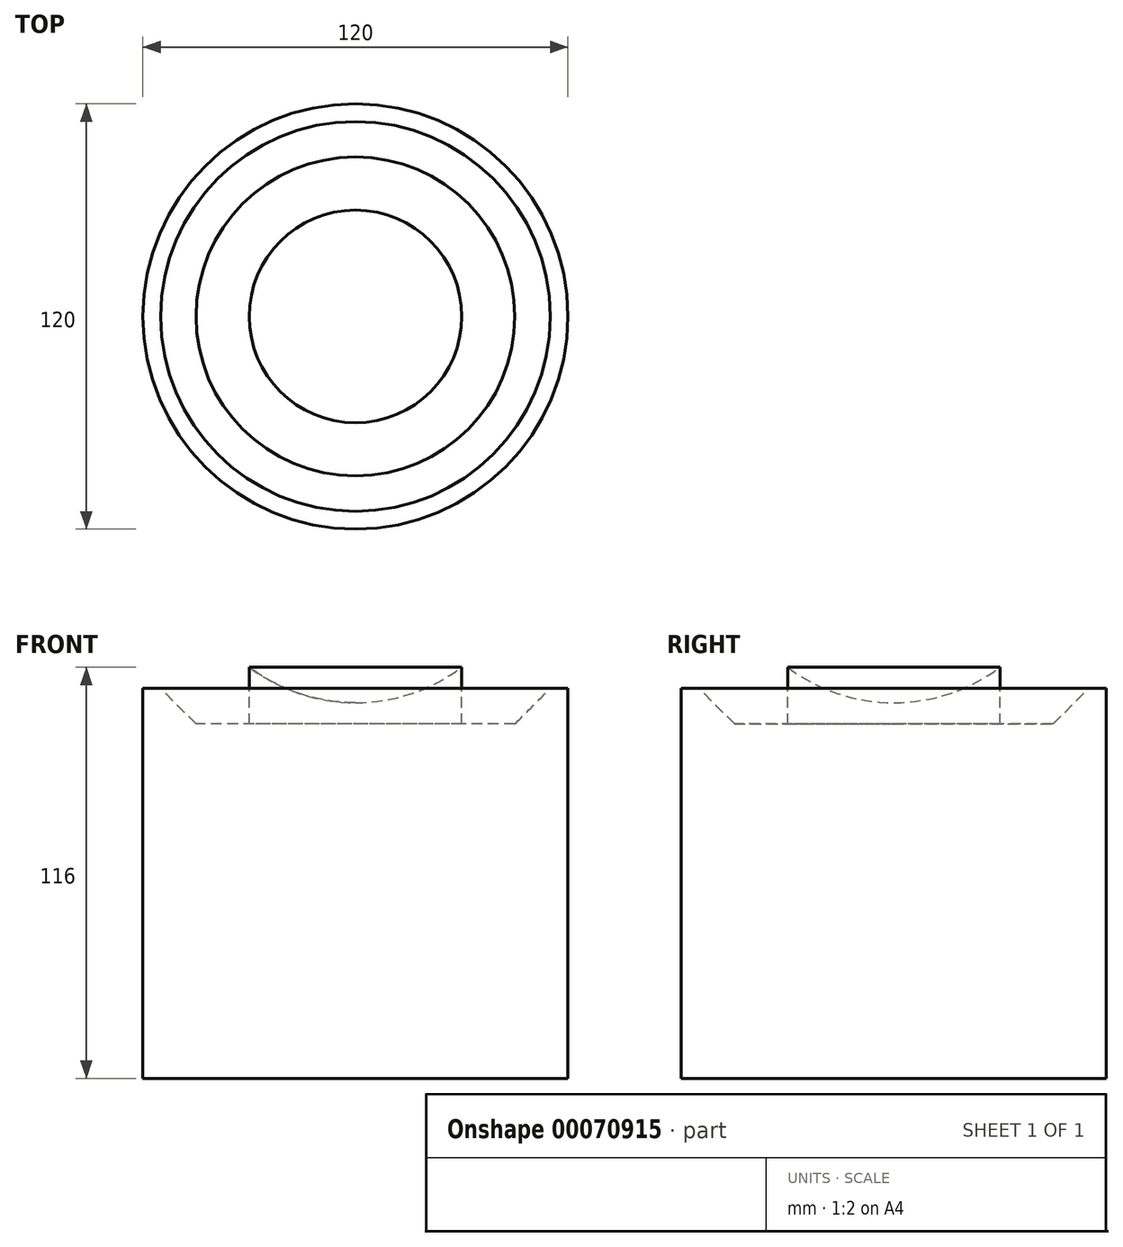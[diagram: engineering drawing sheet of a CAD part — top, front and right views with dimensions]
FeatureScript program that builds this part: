
annotation { "Feature Type Name" : "Feature", "Feature Type Description" : "" }
export const myFeature = defineFeature(function(context is Context, id is Id, definition is map)
    precondition{}
    {
        {
            var Q0;
            Q0=qCreatedBy(makeId("Front.planeOp"),FACE);
            var sketch = newSketch(context, id + "F0", { "sketchPlane" : qUnion([Q0])});
            skArc(sketch, "E0", {"start": v(0, -50) * mm, "mid": v(-50, 0) * mm, "end": v(0, 50) * mm});
            skLineSegment(sketch, "E1", {"start": v(0, 50) * mm, "end": v(0, -56) * mm});
            skLineSegment(sketch, "E2", {"start": v(0, -56) * mm, "end": v(-30, -56) * mm});
            skLineSegment(sketch, "E3", {"start": v(-30, -56) * mm, "end": v(-30, -40) * mm});
            skLineSegment(sketch, "E4", {"start": v(-30, -56) * mm, "end": v(-60, -56) * mm});
            skLineSegment(sketch, "E5", {"start": v(-60, -56) * mm, "end": v(-60, -156) * mm});
            skLineSegment(sketch, "E6", {"start": v(-60, -156) * mm, "end": v(0, -156) * mm});
            skLineSegment(sketch, "E7", {"start": v(0, -156) * mm, "end": v(0, -56) * mm});
            skLineSegment(sketch, "E8", {"start": v(-60, -56) * mm, "end": v(-60, -46) * mm});
            skLineSegment(sketch, "E9", {"start": v(-60, -46) * mm, "end": v(-55, -46) * mm});
            skLineSegment(sketch, "E10", {"start": v(-55, -46) * mm, "end": v(-45, -56) * mm});
            skSolve(sketch);
        }
        {
            var Q0;
            {var subQ0=sQuery(id+"F0.wireOp",EDGE,"E1");var subQ1=sQuery(id+"F0.wireOp",EDGE,"E0");var subQ2=makeQuery(id+"F0.imprint","INTERSECT",VERTEX,{"disambiguationData":[OD(0.0)],"derivedFrom":[subQ1,subQ0]});Q0=makeQuery(id+"F0.imprint","IMPRINT",FACE,{"disambiguationData":[TD([[makeQuery(id+"F0.imprint","IMPRINT",EDGE,{"disambiguationData":[TD([[subQ2,-1.0]])],"derivedFrom":subQ1}),-1.0]])]});}
            var Q1;
            {var subQ4=sQuery(id+"F0.wireOp",EDGE,"E2");Q1=makeQuery(id+"F0.imprint","IMPRINT",FACE,{"disambiguationData":[TD([[makeQuery(id+"F0.imprint","IMPRINT",EDGE,{"derivedFrom":subQ4}),-1.0]])]});}
            var Q2;
            Q2=makeQuery(id+"F0.imprint","IMPRINT",FACE,{"disambiguationData":[TD([[makeQuery(id+"F0.imprint","IMPRINT",EDGE,{"derivedFrom":sQuery(id+"F0.wireOp",EDGE,"E4")}),-1.0]])]});
            var Q3;
            Q3=makeQuery(id+"F0.imprint","IMPRINT",FACE,{"disambiguationData":[TD([[makeQuery(id+"F0.imprint","IMPRINT",EDGE,{"derivedFrom":sQuery(id+"F0.wireOp",EDGE,"E2")}),1.0]])]});
            var Q4;
            Q4=sQuery(id+"F0.wireOp",EDGE,"E1");
            revolve(context, id + "F1", {"entities" : qUnion([Q0, Q1, Q2, Q3]), "axis" : qUnion([Q4]), "revolveType" : RevolveType.FULL});
        }
    });
